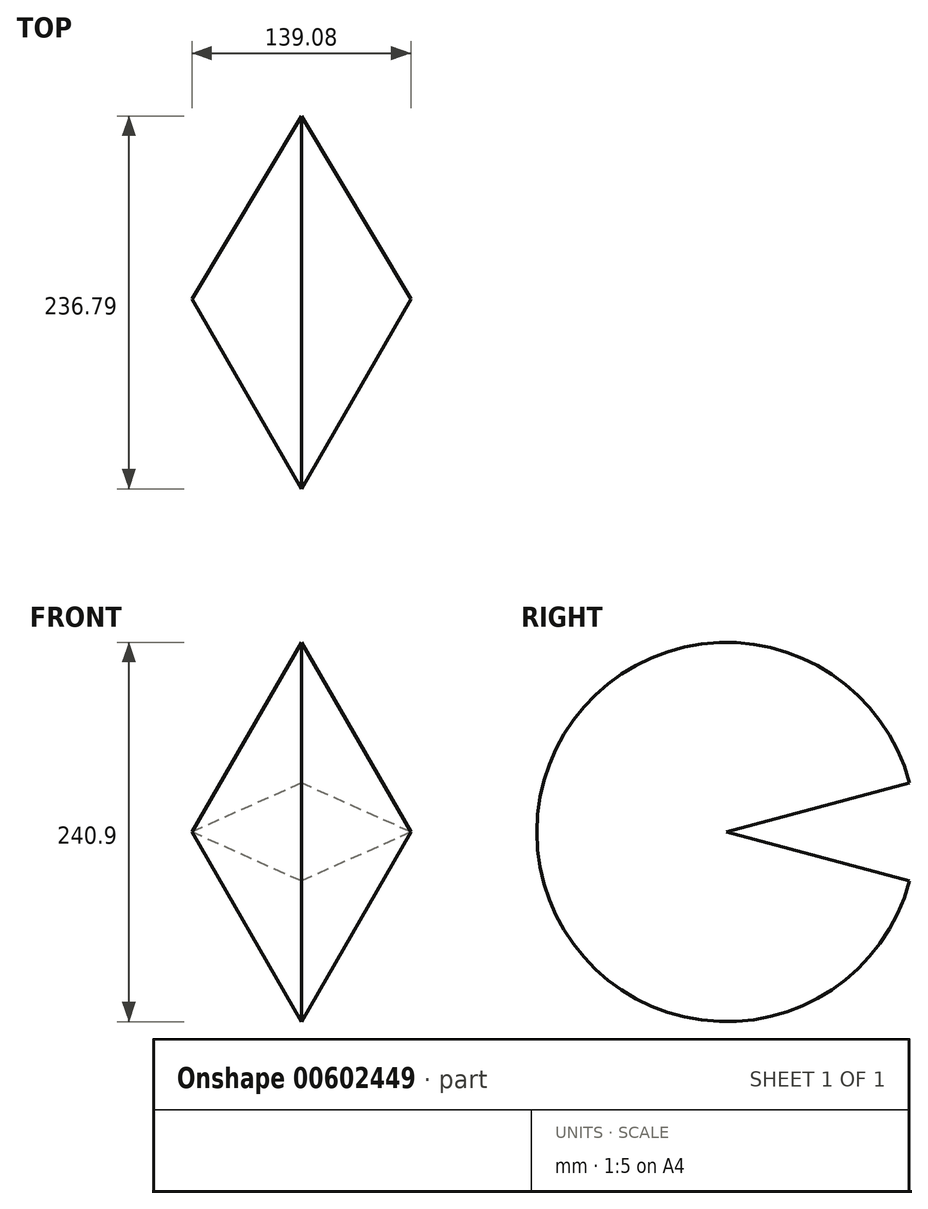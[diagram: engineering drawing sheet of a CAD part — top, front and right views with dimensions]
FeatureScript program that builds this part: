
annotation { "Feature Type Name" : "Feature", "Feature Type Description" : "" }
export const myFeature = defineFeature(function(context is Context, id is Id, definition is map)
    precondition{}
    {
        {
            var Q0;
            Q0=qCreatedBy(makeId("Top.planeOp"),FACE);
            var sketch = newSketch(context, id + "F0", { "sketchPlane" : qUnion([Q0])});
            skCircle(sketch, "E0.cCircle", {"center": v(0, -40.15) * mm, "radius": 40.15 * mm, "construction": true});
            skLineSegment(sketch, "E0.0", {"start": v(-69.54, 0) * mm, "end": v(69.54, 0) * mm});
            skLineSegment(sketch, "E0.1", {"start": v(69.54, 0) * mm, "end": v(0, -120.45) * mm});
            skLineSegment(sketch, "E0.2", {"start": v(0, -120.45) * mm, "end": v(-69.54, 0) * mm});
            skPoint(sketch, "E0.0.midPoint", {"position": v(0, 0) * mm});
            skSolve(sketch);
        }
        {
            var Q0;
            Q0 = qSketchRegion(id + "F0", true);
            var Q1;
            Q1=sQuery(id+"F0.wireOp",EDGE,"E0.0");
            revolve(context, id + "F1", {"entities" : qUnion([Q0]), "axis" : qUnion([Q1]), "revolveType" : RevolveType.SYMMETRIC, "oppositeDirection" : true, "angle" : 330 * degree});
        }
    });
